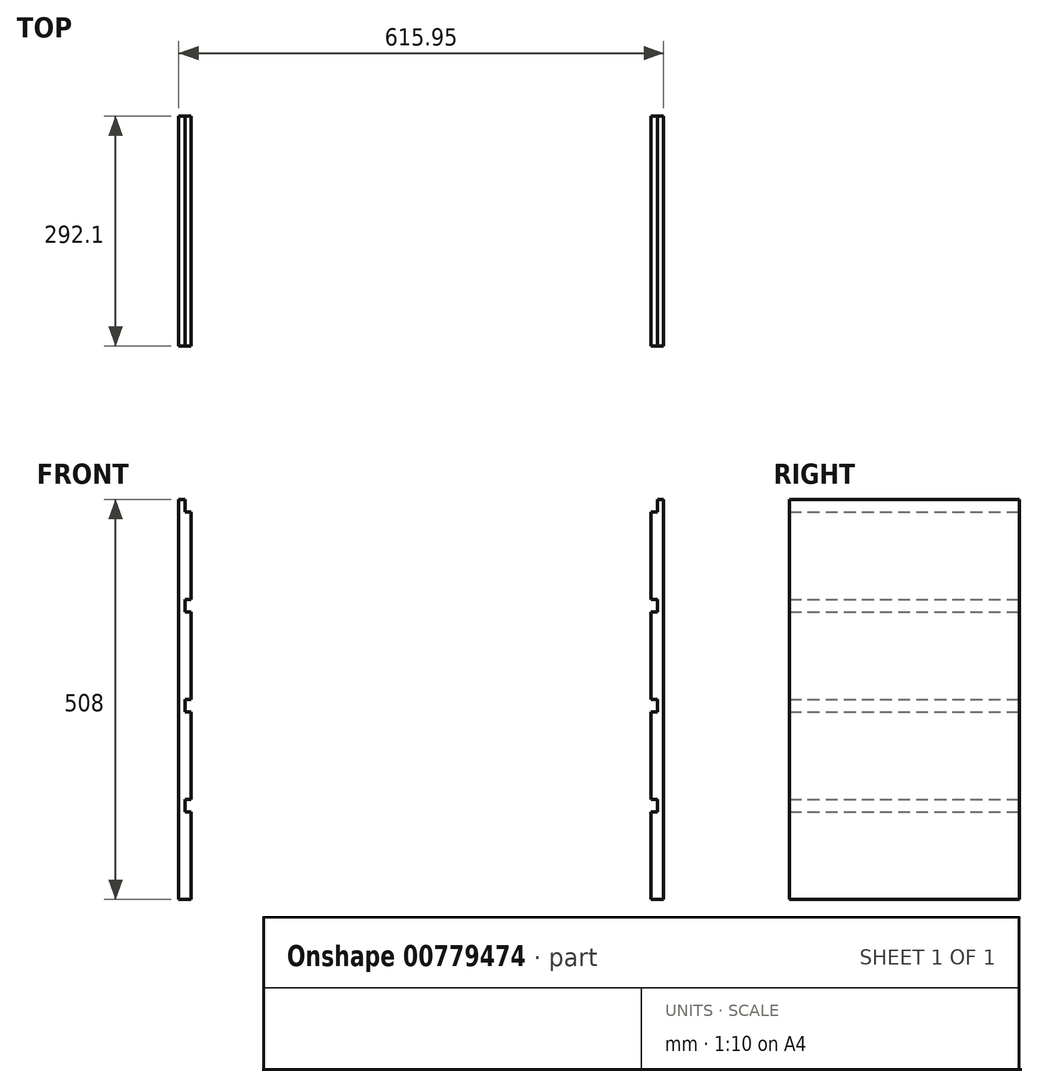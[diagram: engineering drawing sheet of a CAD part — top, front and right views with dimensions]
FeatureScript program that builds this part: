
annotation { "Feature Type Name" : "Feature", "Feature Type Description" : "" }
export const myFeature = defineFeature(function(context is Context, id is Id, definition is map)
    precondition{}
    {
        {
            var Q0;
            Q0=qCreatedBy(makeId("Front.planeOp"),FACE);
            var sketch = newSketch(context, id + "F0", { "sketchPlane" : qUnion([Q0])});
            skLineSegment(sketch, "E0.bottom", {"start": v(0, 508) * mm, "end": v(7.94, 508) * mm});
            skLineSegment(sketch, "E0.top", {"start": v(0, 0) * mm, "end": v(15.88, 0) * mm});
            skLineSegment(sketch, "E0.left", {"start": v(0, 508) * mm, "end": v(0, 0) * mm});
            skLineSegment(sketch, "E0.right", {"start": v(15.87, 492.12) * mm, "end": v(15.87, 381) * mm});
            skLineSegment(sketch, "E1.top", {"start": v(15.87, 492.12) * mm, "end": v(7.94, 492.12) * mm});
            skLineSegment(sketch, "E1.right", {"start": v(7.94, 508) * mm, "end": v(7.94, 492.12) * mm});
            skLineSegment(sketch, "E2.bottom", {"start": v(15.88, 381) * mm, "end": v(7.94, 381) * mm});
            skLineSegment(sketch, "E2.top", {"start": v(15.87, 365.13) * mm, "end": v(7.94, 365.13) * mm});
            skLineSegment(sketch, "E2.right", {"start": v(7.94, 381) * mm, "end": v(7.94, 365.13) * mm});
            skLineSegment(sketch, "E3.bottom", {"start": v(15.88, 254) * mm, "end": v(7.94, 254) * mm});
            skLineSegment(sketch, "E3.top", {"start": v(15.87, 238.13) * mm, "end": v(7.94, 238.13) * mm});
            skLineSegment(sketch, "E3.right", {"start": v(7.94, 254) * mm, "end": v(7.94, 238.12) * mm});
            skLineSegment(sketch, "E4.bottom", {"start": v(15.88, 127) * mm, "end": v(7.94, 127) * mm});
            skLineSegment(sketch, "E4.top", {"start": v(15.87, 111.12) * mm, "end": v(7.94, 111.12) * mm});
            skLineSegment(sketch, "E4.right", {"start": v(7.94, 127) * mm, "end": v(7.94, 111.12) * mm});
            skLineSegment(sketch, "E5", {"start": v(7.94, 111.12) * mm, "end": v(7.94, 0) * mm, "construction": true});
            skLineSegment(sketch, "E6", {"start": v(7.94, 127) * mm, "end": v(7.94, 238.12) * mm, "construction": true});
            skLineSegment(sketch, "E7", {"start": v(7.94, 254) * mm, "end": v(7.94, 365.13) * mm, "construction": true});
            skLineSegment(sketch, "E8", {"start": v(7.94, 381) * mm, "end": v(7.94, 492.12) * mm, "construction": true});
            skLineSegment(sketch, "E9.trimOffspring", {"start": v(15.87, 111.13) * mm, "end": v(15.88, 0) * mm});
            skLineSegment(sketch, "E10.trimOffspring", {"start": v(15.87, 238.13) * mm, "end": v(15.87, 127) * mm});
            skLineSegment(sketch, "E11.trimOffspring", {"start": v(15.87, 365.13) * mm, "end": v(15.87, 254) * mm});
            skLineSegment(sketch, "E12", {"start": v(15.88, 111.12) * mm, "end": v(15.88, 127) * mm, "construction": true});
            skLineSegment(sketch, "E13", {"start": v(15.87, 238.13) * mm, "end": v(15.87, 254) * mm, "construction": true});
            skLineSegment(sketch, "E14", {"start": v(15.87, 365.13) * mm, "end": v(15.87, 381) * mm, "construction": true});
            skLineSegment(sketch, "E15", {"start": v(15.87, 492.12) * mm, "end": v(15.87, 508) * mm, "construction": true});
            skLineSegment(sketch, "E16", {"start": v(15.87, 508) * mm, "end": v(7.94, 508) * mm, "construction": true});
            skSolve(sketch);
        }
        {
            var Q0;
            Q0 = qSketchRegion(id + "F0", true);
            extrude(context, id + "F1", {"entities" : qUnion([Q0]), "endBound" : BoundingType.SYMMETRIC, "depth" : 292.1 * mm, "offsetDistance" : 25.4 * mm});
        }
        {
            var Q0;
            Q0=makeQuery(id+"F1.opExtrude","SWEPT_FACE",FACE,{"disambiguationData":[OSD([sQuery(id+"F0.wireOp",EDGE,"E9.trimOffspring")])]});
            cPlane(context, id + "F2", {"entities" : qUnion([Q0]), "cplaneType" : CPlaneType.OFFSET, "offset" : 292.1 * mm, "width" : 152.4 * mm, "height" : 152.4 * mm});
        }
        {
            var Q0;
            Q0=makeQuery(id+"F1.opExtrude","SWEPT_BODY",BODY,{"disambiguationData":[OSD([sQuery(id+"F0.wireOp",EDGE,"E0.bottom"),sQuery(id+"F0.wireOp",EDGE,"E0.top"),sQuery(id+"F0.wireOp",EDGE,"E0.left"),sQuery(id+"F0.wireOp",EDGE,"E0.right"),sQuery(id+"F0.wireOp",EDGE,"E1.top"),sQuery(id+"F0.wireOp",EDGE,"E1.right"),sQuery(id+"F0.wireOp",EDGE,"E2.bottom"),sQuery(id+"F0.wireOp",EDGE,"E2.top"),sQuery(id+"F0.wireOp",EDGE,"E2.right"),sQuery(id+"F0.wireOp",EDGE,"E3.bottom"),sQuery(id+"F0.wireOp",EDGE,"E3.top"),sQuery(id+"F0.wireOp",EDGE,"E3.right"),sQuery(id+"F0.wireOp",EDGE,"E4.bottom"),sQuery(id+"F0.wireOp",EDGE,"E4.top"),sQuery(id+"F0.wireOp",EDGE,"E4.right"),sQuery(id+"F0.wireOp",EDGE,"E9.trimOffspring"),sQuery(id+"F0.wireOp",EDGE,"E10.trimOffspring"),sQuery(id+"F0.wireOp",EDGE,"E11.trimOffspring")])]});
            var Q1;
            Q1=qCreatedBy(id+"F2.planeOp",FACE);
            mirror(context, id + "F3", {"entities" : qUnion([Q0]), "mirrorPlane" : qUnion([Q1])});
        }
    });
